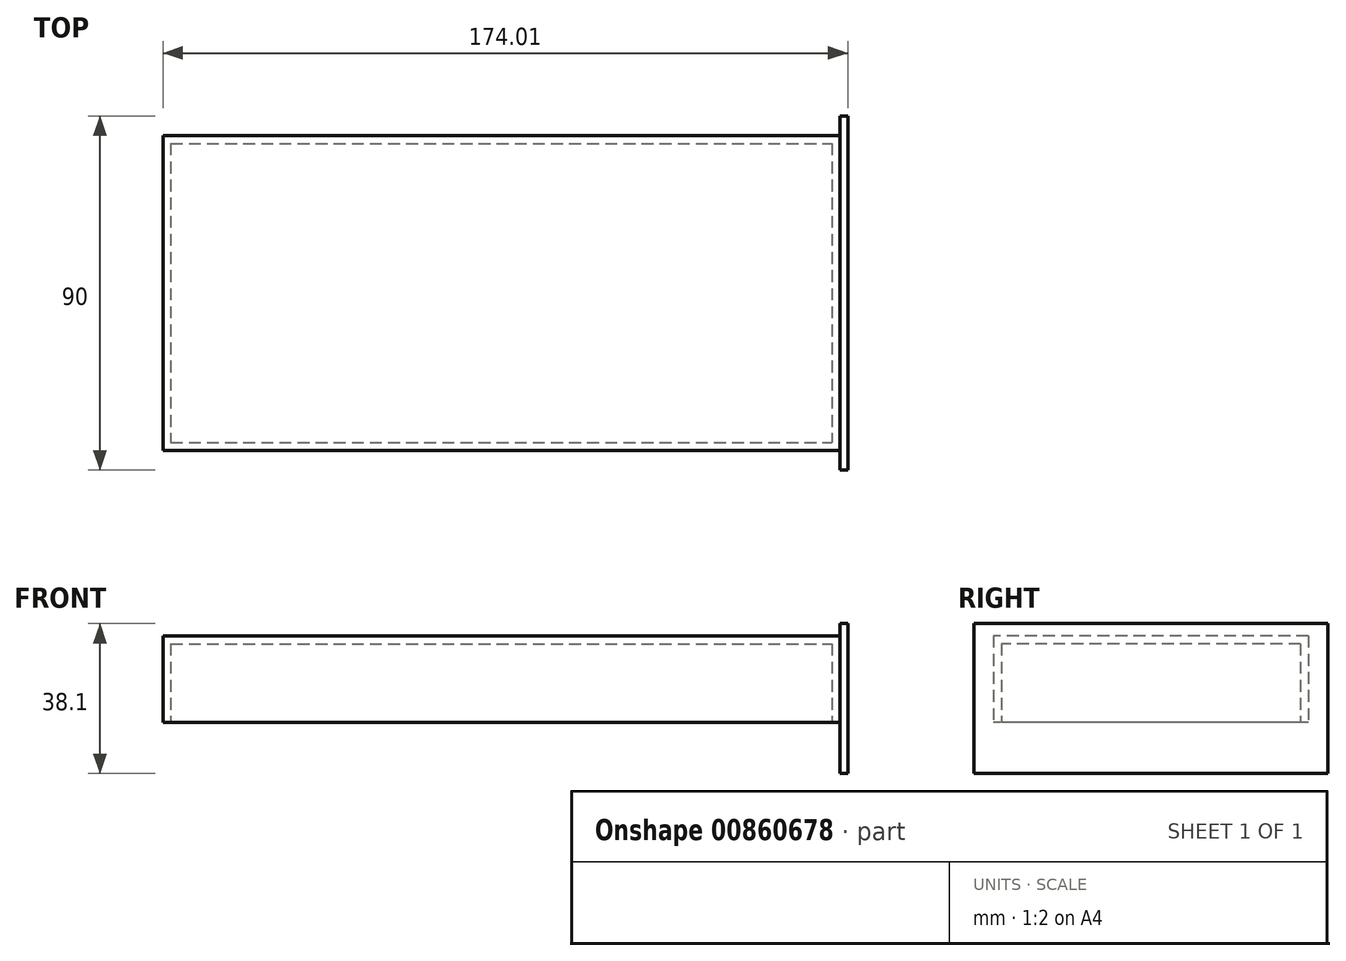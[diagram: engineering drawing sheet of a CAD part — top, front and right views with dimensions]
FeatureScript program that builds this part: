
annotation { "Feature Type Name" : "Feature", "Feature Type Description" : "" }
export const myFeature = defineFeature(function(context is Context, id is Id, definition is map)
    precondition{}
    {
        {
            var Q0;
            Q0=qCreatedBy(makeId("Top.planeOp"),FACE);
            var sketch = newSketch(context, id + "F0", { "sketchPlane" : qUnion([Q0])});
            skLineSegment(sketch, "E0.bottom", {"start": v(-83.22, 31.58) * mm, "end": v(88.78, 31.58) * mm});
            skLineSegment(sketch, "E0.top", {"start": v(-83.22, -48.42) * mm, "end": v(88.78, -48.42) * mm});
            skLineSegment(sketch, "E0.left", {"start": v(-83.22, 31.58) * mm, "end": v(-83.22, -48.42) * mm});
            skLineSegment(sketch, "E0.right", {"start": v(88.78, 31.58) * mm, "end": v(88.78, -48.42) * mm});
            skSolve(sketch);
        }
        {
            var Q0;
            Q0=makeQuery(id+"F0.imprint","IMPRINT",FACE,{"disambiguationData":[TD([[makeQuery(id+"F0.imprint","IMPRINT",EDGE,{"derivedFrom":sQuery(id+"F0.wireOp",EDGE,"E0.bottom")}),-1.0]])]});
            extrude(context, id + "F1", {"entities" : qUnion([Q0]), "depth" : 22 * mm, "offsetDistance" : 25 * mm});
        }
        {
            var Q0;
            Q0=makeQuery(id+"F1.opExtrude","CAP_FACE",FACE,{"disambiguationData":[OSD([sQuery(id+"F0.wireOp",EDGE,"E0.bottom"),sQuery(id+"F0.wireOp",EDGE,"E0.top"),sQuery(id+"F0.wireOp",EDGE,"E0.left"),sQuery(id+"F0.wireOp",EDGE,"E0.right")])],"isStart":true});
            shell(context, id + "F2", {"entities" : qUnion([Q0]), "thickness" : 2 * mm});
        }
        {
            var Q0;
            Q0=qCreatedBy(makeId("Top.planeOp"),FACE);
            var sketch = newSketch(context, id + "F3", { "sketchPlane" : qUnion([Q0])});
            skLineSegment(sketch, "E1", {"start": v(88.79, -53.42) * mm, "end": v(88.79, 36.58) * mm});
            skLineSegment(sketch, "E2", {"start": v(88.79, 36.58) * mm, "end": v(90.79, 36.58) * mm});
            skLineSegment(sketch, "E3", {"start": v(90.79, -53.42) * mm, "end": v(88.79, -53.42) * mm});
            skLineSegment(sketch, "E4", {"start": v(90.79, 36.58) * mm, "end": v(90.79, -53.42) * mm});
            skSolve(sketch);
        }
        {
            var Q0;
            Q0=makeQuery(id+"F3.imprint","IMPRINT",FACE,{"disambiguationData":[TD([[makeQuery(id+"F3.imprint","IMPRINT",EDGE,{"derivedFrom":sQuery(id+"F3.wireOp",EDGE,"E1")}),-1.0]])]});
            extrude(context, id + "F4", {"entities" : qUnion([Q0]), "depth" : 22.1 * mm, "offsetDistance" : 25 * mm});
        }
        {
            var Q0;
            Q0=makeQuery(id+"F4.opExtrude","CAP_FACE",FACE,{"disambiguationData":[OSD([sQuery(id+"F3.wireOp",EDGE,"E1"),sQuery(id+"F3.wireOp",EDGE,"E2"),sQuery(id+"F3.wireOp",EDGE,"E3"),sQuery(id+"F3.wireOp",EDGE,"E4")])],"isStart":true});
            extrude(context, id + "F5", {"entities" : qUnion([Q0]), "operationType" : NewBodyOperationType.ADD, "depth" : 3 * mm, "offsetDistance" : 25 * mm});
        }
        {
            var Q0;
            Q0=makeQuery(id+"F4.opExtrude","CAP_FACE",FACE,{"disambiguationData":[OSD([sQuery(id+"F3.wireOp",EDGE,"E1"),sQuery(id+"F3.wireOp",EDGE,"E2"),sQuery(id+"F3.wireOp",EDGE,"E3"),sQuery(id+"F3.wireOp",EDGE,"E4")])],"isStart":false});
            extrude(context, id + "F6", {"entities" : qUnion([Q0]), "operationType" : NewBodyOperationType.ADD, "depth" : 3 * mm, "offsetDistance" : 25 * mm});
        }
        {
            var Q0;
            Q0=makeQuery(id+"F5.opExtrude","CAP_FACE",FACE,{"disambiguationData":[OSD([sQuery(id+"F3.wireOp",EDGE,"E1"),sQuery(id+"F3.wireOp",EDGE,"E2"),sQuery(id+"F3.wireOp",EDGE,"E3"),sQuery(id+"F3.wireOp",EDGE,"E4")])],"isStart":false});
            extrude(context, id + "F7", {"entities" : qUnion([Q0]), "operationType" : NewBodyOperationType.ADD, "depth" : 10 * mm, "offsetDistance" : 25 * mm});
        }
    });
